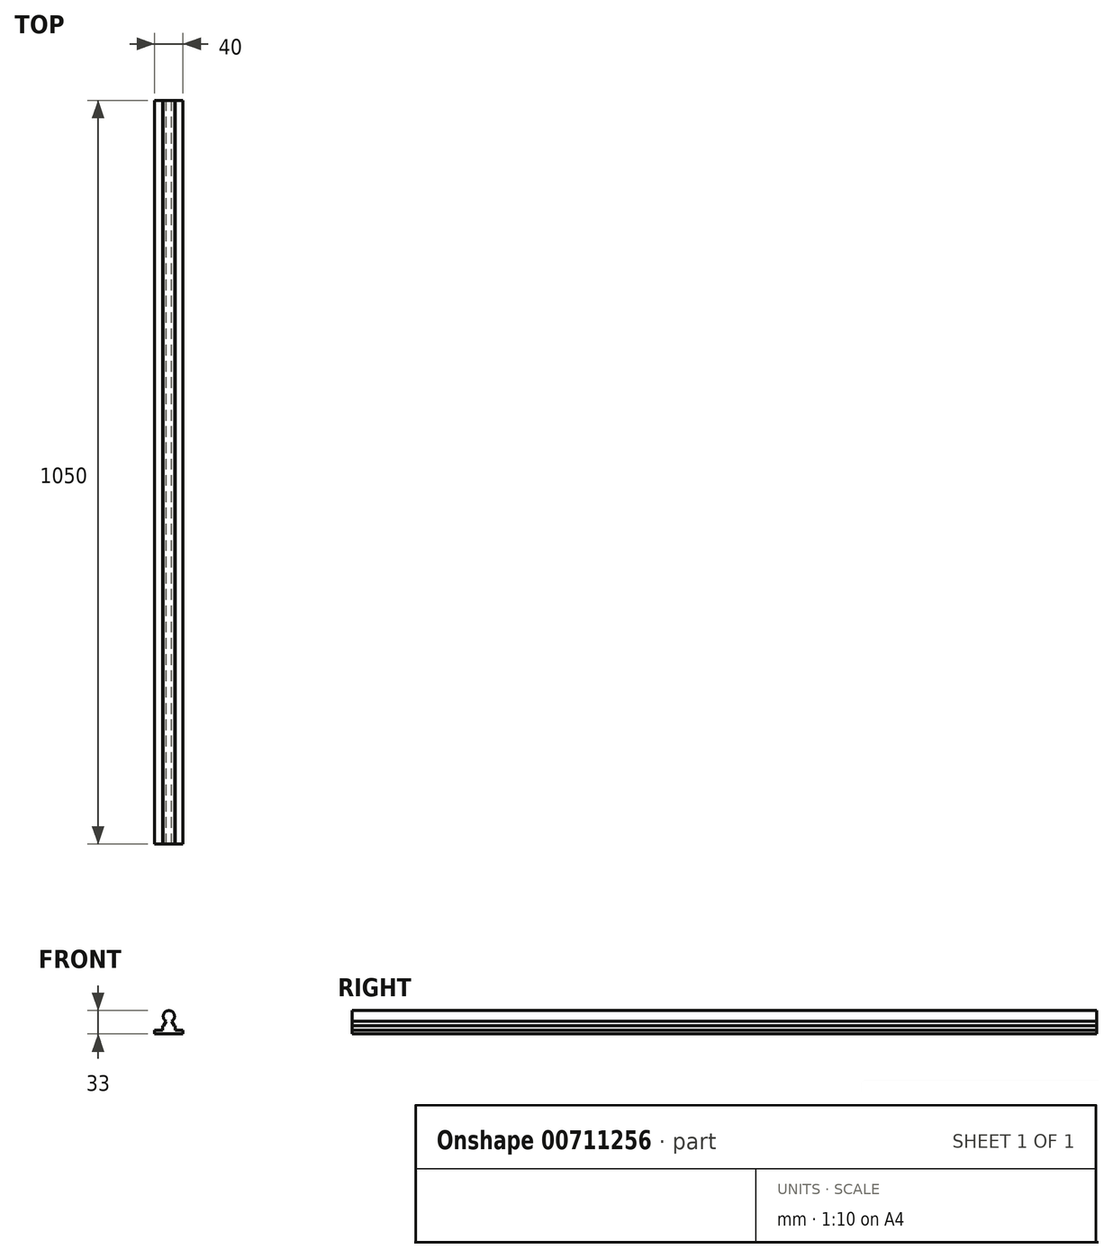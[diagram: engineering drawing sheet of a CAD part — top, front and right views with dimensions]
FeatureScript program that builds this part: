
annotation { "Feature Type Name" : "Feature", "Feature Type Description" : "" }
export const myFeature = defineFeature(function(context is Context, id is Id, definition is map)
    precondition{}
    {
        {
            var Q0;
            Q0=qCreatedBy(makeId("Front.planeOp"),FACE);
            var sketch = newSketch(context, id + "F0", { "sketchPlane" : qUnion([Q0])});
            skLineSegment(sketch, "E0.top", {"start": v(20, -2.5) * mm, "end": v(-20, -2.5) * mm});
            skLineSegment(sketch, "E0.left", {"start": v(20, 2.5) * mm, "end": v(20, -2.5) * mm});
            skLineSegment(sketch, "E0.right", {"start": v(-20, 2.5) * mm, "end": v(-20, -2.5) * mm});
            skPoint(sketch, "E0.middle", {"position": v(0, 0) * mm});
            skArc(sketch, "E1", {"start": v(4, 15.57) * mm, "mid": v(0, 30.5) * mm, "end": v(-4, 15.57) * mm});
            skLineSegment(sketch, "E2", {"start": v(-20, 2.5) * mm, "end": v(-8.9, 2.5) * mm});
            skLineSegment(sketch, "E3", {"start": v(20, 2.5) * mm, "end": v(8.9, 2.5) * mm});
            skLineSegment(sketch, "E4", {"start": v(-8.9, 2.5) * mm, "end": v(-8.9, 9.2) * mm});
            skLineSegment(sketch, "E5", {"start": v(8.9, 2.5) * mm, "end": v(8.9, 9.2) * mm});
            skLineSegment(sketch, "E6", {"start": v(-8.9, 9.2) * mm, "end": v(-7.68, 9.2) * mm});
            skLineSegment(sketch, "E7", {"start": v(8.9, 9.2) * mm, "end": v(7.68, 9.2) * mm});
            skLineSegment(sketch, "E8", {"start": v(-7.68, 9.2) * mm, "end": v(-4, 15.57) * mm});
            skLineSegment(sketch, "E9", {"start": v(7.68, 9.2) * mm, "end": v(4, 15.57) * mm});
            skLineSegment(sketch, "E10.trimOffspring", {"start": v(-8.9, 2.5) * mm, "end": v(-20, 2.5) * mm});
            skSolve(sketch);
        }
        {
            var Q0;
            Q0=makeQuery(id+"F0.imprint","IMPRINT",FACE,{"disambiguationData":[TD([[makeQuery(id+"F0.imprint","IMPRINT",EDGE,{"derivedFrom":sQuery(id+"F0.wireOp",EDGE,"E0.top")}),-1.0]])]});
            extrude(context, id + "F1", {"entities" : qUnion([Q0]), "endBound" : BoundingType.SYMMETRIC, "depth" : 1050 * mm, "offsetDistance" : 25 * mm});
        }
    });
